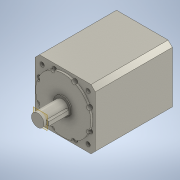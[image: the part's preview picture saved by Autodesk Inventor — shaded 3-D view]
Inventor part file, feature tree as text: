
AUTODESK INVENTOR PART (.ipt)
format: ipt  version: 2022.1 (Build 261234000, 234)  size: 239,616 bytes
history: native  units: in
note: dims shown in document units (in); Inventor stores cm internally (conversion verified against a paired STEP export)
features: extrude x10, sketch x10, plane x1, chamfer x1
ambient origin geometry x8: Origin, YZ Plane, XZ Plane, XY Plane, X Axis, Y Axis, Z Axis, Center Point
bodies: Solid1 (feature_tree)
feature tree (22):
  extrude  "Extrusion1"  Depth=4.7244in
  extrude  "Extrusion2"  Depth=4.3307in
  extrude  "Extrusion3"  Depth=0.1575in
  extrude  "Extrusion4"  Depth=0.0787in
  extrude  "Extrusion5"  Depth=1.9291in
  extrude  "Extrusion6"  Depth=1.5748in TaperAngle=360.0deg
  plane  "Work Plane1"
  extrude  "Extrusion7"  Depth=1.9685in
  extrude  "Extrusion8"  Depth=4.3307in
  extrude  "Extrusion9"  Depth=1.9685in TaperAngle=0.0deg
  extrude  "Extrusion10"  Depth=0.315in
  chamfer  "Chamfer1"  Distance=0.315in
  sketch  "Sketch1"  dims[d0=4.7244in d1=4.7244in]
  sketch  "Sketch2"  dims[d2=6.063in d3=0.0in d4=4.3307in]
  sketch  "Sketch3"  dims[d5=0.1575in d6=0.0in d7=1.378in]
  sketch  "Sketch4"  dims[d8=0.0787in d9=0.0in d10=0.9843in]
  sketch  "Sketch5"  dims[d11=1.9291in d12=0.0in d13=0.3346in]
  sketch  "Sketch6"  dims[d14=5.1181in d15=1.5748in d17=360.0deg]
  sketch  "Sketch7"  dims[d19=1.9685in d20=0.0in d21=0.3346in]
  sketch  "Sketch8"  dims[d22=22.5deg d23=4.3307in]
  sketch  "Sketch9"  dims[d24=3.1496in d26=360.0deg d28=1.9685in d29=0.0in]
  sketch  "Sketch10"  dims[d30=-0.1969in d31=0.315in d32=0.315in d33=1.5748in d34=0.0in d35=0.748in d36=1.5748in d37=0.0in d38=3.7402in d39=0.1181in d40=0.0in d41=4.9213in d42=0.374in d43=1.5748in d45=360.0deg d47=1.9685in d48=0.0in d49=0.3346in d50=0.0787in d51=45.0deg]
